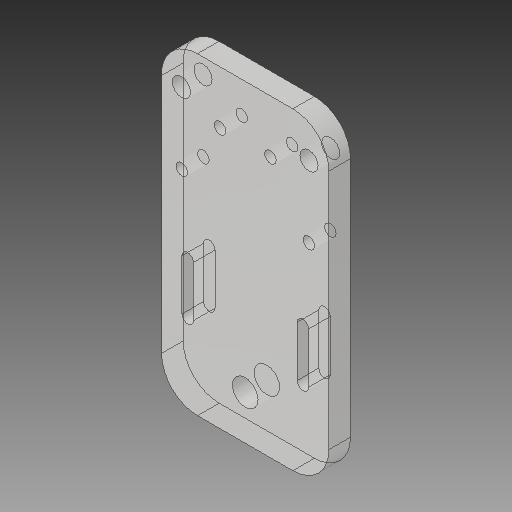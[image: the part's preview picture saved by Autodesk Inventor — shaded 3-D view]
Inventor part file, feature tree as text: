
AUTODESK INVENTOR PART (.ipt)
format: ipt  version: 2018 (Build 220112000, 112)  size: 200,704 bytes
history: native  units: mm
features: other x3, sketch x2
ambient origin geometry x8: Origin, YZ Plane, XZ Plane, XY Plane, X Axis, Y Axis, Z Axis, Center Point
bodies: Solid1 (feature_tree)
feature tree (5):
  other  "Hotend Front Plate revised.ipt"
  other  "Solid1::Hotend Front Plate revised.ipt"
  other  "TaggingFeature1"
  sketch  "Sketch1"  dims[d0=10.0mm]
  sketch  "Sketch2"
